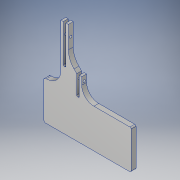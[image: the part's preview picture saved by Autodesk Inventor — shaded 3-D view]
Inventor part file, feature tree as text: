
AUTODESK INVENTOR PART (.ipt)
format: ipt  version: 2017 (Build 210142000, 142)  size: 242,688 bytes
history: native  units: in
note: dims shown in document units (in); Inventor stores cm internally (conversion verified against a paired STEP export)
features: sketch x15, extrude x12, fillet x5
ambient origin geometry x8: Origin, YZ Plane, XZ Plane, XY Plane, X Axis, Y Axis, Z Axis, Center Point
bodies: Solid1 (feature_tree)
feature tree (32):
  extrude  "Extrusion1"  Depth=2.0in
  sketch  "Sketch2"  dims[d3=4.5in d4=0.125in d5=0.0in]
  extrude  "Extrusion2"  Depth=0.125in TaperAngle=0.0deg
  extrude  "Extrusion3"  Depth=0.066in
  extrude  "Extrusion4"  Depth=0.25in
  extrude  "Extrusion5"  Depth=0.125in TaperAngle=0.0deg
  extrude  "Extrusion6"  Depth=3.0in TaperAngle=0.0deg
  sketch  "Sketch6"  dims[d14=3.0in d15=0.0in d16=3.0in d17=0.0in]
  sketch  "Sketch7"  dims[d18=0.75in d19=0.125in]
  sketch  "Sketch8"  dims[d20=2.0in d21=0.0in d22=1.64in]
  sketch  "Sketch9"  dims[d23=0.125in d24=2.0in d25=0.0in]
  extrude  "Extrusion11"  Depth=0.125in
  extrude  "Extrusion12"  Depth=2.0in
  extrude  "Extrusion13"  Depth=2.0in TaperAngle=0.0deg
  extrude  "Extrusion14"  Depth=0.125in
  extrude  "Extrusion15"  Depth=0.125in
  extrude  "Extrusion16"  Depth=0.125in
  fillet  "Fillet1"  Radius=0.25in
  fillet  "Fillet3"  Radius=0.067in
  fillet  "Fillet4"  Radius=0.125in
  fillet  "Fillet5"  Radius=0.25in
  fillet  "Fillet6"  Radius=0.125in
  sketch  "Sketch1"  dims[d1=4.5in d2=2.0in]
  sketch  "Sketch3"  dims[d7=0.066in d8=0.066in]
  sketch  "Sketch4"  dims[d9=0.125in d10=0.25in]
  sketch  "Sketch5"  dims[d11=0.125in d12=0.125in d13=0.0in]
  sketch  "Sketch12"  dims[d30=0.125in d34=0.125in]
  sketch  "Sketch13"  dims[d35=0.132in d36=0.125in]
  sketch  "Sketch14"  dims[d44=0.067in d45=0.125in d46=0.25in d47=0.0in d48=0.067in d49=0.125in d50=0.25in d51=0.0in d52=0.125in]
  sketch  "Sketch15"  dims[d55=0.25in d56=0.0in]
  sketch  "Sketch16"  dims[d57=2.0in d58=0.0in]
  sketch  "Sketch17"  dims[d59=0.25in d60=0.0in d61=0.5in d62=0.0in d63=0.0625in d65=1.0in d67=0.625in d68=0.0625in d69=0.75in]
